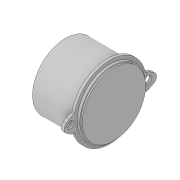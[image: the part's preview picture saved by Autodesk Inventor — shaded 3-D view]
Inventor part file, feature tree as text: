
AUTODESK INVENTOR PART (.ipt)
format: ipt  version: 2019 (Build 230136000, 136)  size: 139,264 bytes
history: native  units: mm
features: sketch x6, extrude x5, fillet x1
ambient origin geometry x8: Origin, YZ Plane, XZ Plane, XY Plane, X Axis, Y Axis, Z Axis, Center Point
bodies: Solid1 (feature_tree)
feature tree (12):
  extrude  "Extrusion1"  Depth=16.0mm TaperAngle=0.0deg
  extrude  "Extrusion2"  Depth=2.0mm
  fillet  "Fillet1"  Radius=1.0mm
  extrude  "Extrusion3"  Depth=0.5mm TaperAngle=0.0deg
  extrude  "Extrusion4"  [1 undecoded]
  sketch  "Sketch5"
  extrude  "Extrusion5"  [1 undecoded]
  sketch  "Sketch1"  dims[d0=25.0mm d1=16.0mm d2=0.0mm]
  sketch  "Sketch2"  dims[d3=1.0mm d4=0.0mm d5=2.0mm d6=1.0mm d7=0.0mm]
  sketch  "Sketch3"  dims[d8=1.0mm d9=0.0mm d10=0.5mm d11=0.0mm]
  sketch  "Sketch4"
  sketch  "Sketch6"
note: 2 required parameter values undecoded (feature->parameter linkage not recoverable at this tier; creation-order binding heuristic only, values carry confidence <= 0.55)
